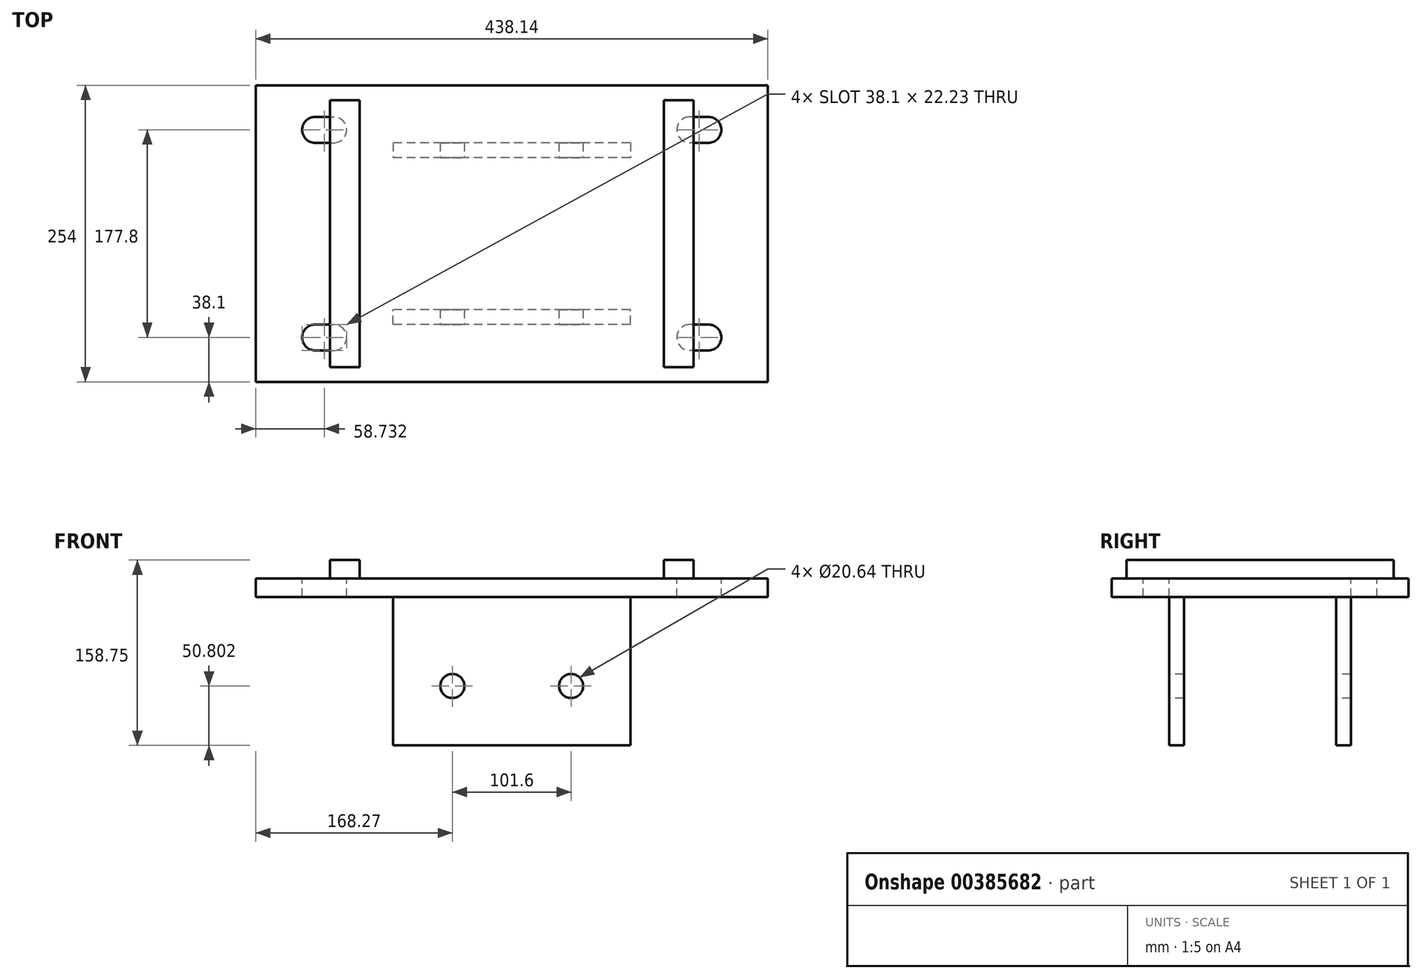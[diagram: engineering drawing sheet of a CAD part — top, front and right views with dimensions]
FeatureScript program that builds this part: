
annotation { "Feature Type Name" : "Feature", "Feature Type Description" : "" }
export const myFeature = defineFeature(function(context is Context, id is Id, definition is map)
    precondition{}
    {
        {
            var Q0;
            Q0=qCreatedBy(makeId("Top.planeOp"),FACE);
            var sketch = newSketch(context, id + "F0", { "sketchPlane" : qUnion([Q0])});
            skLineSegment(sketch, "E0.bottom", {"start": v(219.08, -127) * mm, "end": v(-219.08, -127) * mm});
            skLineSegment(sketch, "E0.top", {"start": v(219.08, 127) * mm, "end": v(-219.08, 127) * mm});
            skLineSegment(sketch, "E0.left", {"start": v(219.08, -127) * mm, "end": v(219.08, 127) * mm});
            skLineSegment(sketch, "E0.right", {"start": v(-219.08, -127) * mm, "end": v(-219.08, 127) * mm});
            skPoint(sketch, "E0.middle", {"position": v(0, 0) * mm});
            skSolve(sketch);
        }
        {
            var Q0;
            Q0 = qSketchRegion(id + "F0", true);
            extrude(context, id + "F1", {"entities" : qUnion([Q0]), "endBound" : BoundingType.SYMMETRIC, "depth" : 15.88 * mm});
        }
        {
            var Q0;
            Q0=qCreatedBy(makeId("Front.planeOp"),FACE);
            var sketch = newSketch(context, id + "F2", { "sketchPlane" : qUnion([Q0])});
            skLineSegment(sketch, "E1.0", {"start": v(219.08, -7.94) * mm, "end": v(-219.08, -7.94) * mm});
            skLineSegment(sketch, "E2.bottom", {"start": v(-101.6, -7.94) * mm, "end": v(101.6, -7.94) * mm});
            skLineSegment(sketch, "E2.top", {"start": v(-101.6, -134.94) * mm, "end": v(101.6, -134.94) * mm});
            skLineSegment(sketch, "E2.left", {"start": v(-101.6, -7.94) * mm, "end": v(-101.6, -134.94) * mm});
            skLineSegment(sketch, "E2.right", {"start": v(101.6, -7.94) * mm, "end": v(101.6, -134.94) * mm});
            skSolve(sketch);
        }
        {
            var Q0;
            Q0 = qSketchRegion(id + "F2", true);
            extrude(context, id + "F3", {"entities" : qUnion([Q0]), "endBound" : BoundingType.SYMMETRIC, "depth" : 12.7 * mm});
        }
        {
            var Q0;
            Q0=makeQuery(id+"F3.opExtrude","SWEPT_BODY",BODY,{"disambiguationData":[OSD([sQuery(id+"F2.wireOp",EDGE,"E2.bottom"),sQuery(id+"F2.wireOp",EDGE,"E2.top"),sQuery(id+"F2.wireOp",EDGE,"E2.left"),sQuery(id+"F2.wireOp",EDGE,"E2.right")])]});
            var Q1;
            Q1=makeQuery(id+"F1.opExtrude","CAP_EDGE",EDGE,{"disambiguationData":[OSD([sQuery(id+"F0.wireOp",EDGE,"E0.left")])],"isStart":true});
            transform(context, id + "F4", {"entities" : qUnion([Q0]), "transformType" : TransformType.TRANSLATION_DISTANCE, "transformDirection" : qUnion([Q1]), "distance" : 71.44 * mm, "oppositeDirection" : true, "makeCopy" : false});
        }
        {
            var Q0;
            Q0=qCreatedBy(makeId("Right.planeOp"),FACE);
            var sketch = newSketch(context, id + "F5", { "sketchPlane" : qUnion([Q0])});
            skLineSegment(sketch, "E3", {"start": v(0, 0) * mm, "end": v(0, 158.38) * mm, "construction": true});
            skSolve(sketch);
        }
        {
            var Q0;
            Q0=makeQuery(id+"F3.opExtrude","SWEPT_BODY",BODY,{"disambiguationData":[OSD([sQuery(id+"F2.wireOp",EDGE,"E2.bottom"),sQuery(id+"F2.wireOp",EDGE,"E2.top"),sQuery(id+"F2.wireOp",EDGE,"E2.left"),sQuery(id+"F2.wireOp",EDGE,"E2.right")])]});
            var Q1;
            Q1=qCreatedBy(makeId("Front.planeOp"),FACE);
            mirror(context, id + "F6", {"operationType" : NewBodyOperationType.ADD, "entities" : qUnion([Q0]), "mirrorPlane" : qUnion([Q1])});
        }
        {
            var Q0;
            Q0=makeQuery(id+"F1.opExtrude","CAP_FACE",FACE,{"disambiguationData":[OSD([sQuery(id+"F0.wireOp",EDGE,"E0.bottom"),sQuery(id+"F0.wireOp",EDGE,"E0.top"),sQuery(id+"F0.wireOp",EDGE,"E0.left"),sQuery(id+"F0.wireOp",EDGE,"E0.right")])],"isStart":false});
            var sketch = newSketch(context, id + "F7", { "sketchPlane" : qUnion([Q0])});
            skLineSegment(sketch, "E4.bottom", {"start": v(-155.58, 114.3) * mm, "end": v(-130.18, 114.3) * mm});
            skLineSegment(sketch, "E4.top", {"start": v(-155.57, -114.3) * mm, "end": v(-130.17, -114.3) * mm});
            skLineSegment(sketch, "E4.left", {"start": v(-155.58, 114.3) * mm, "end": v(-155.58, -114.3) * mm});
            skLineSegment(sketch, "E4.right", {"start": v(-130.18, 114.3) * mm, "end": v(-130.18, -114.3) * mm});
            skLineSegment(sketch, "E5.MirrorCS", {"start": v(155.58, 114.3) * mm, "end": v(130.18, 114.3) * mm});
            skLineSegment(sketch, "E6.MirrorCS", {"start": v(130.18, 114.3) * mm, "end": v(130.18, -114.3) * mm});
            skLineSegment(sketch, "E7.MirrorCS", {"start": v(155.57, -114.3) * mm, "end": v(130.17, -114.3) * mm});
            skLineSegment(sketch, "E8.MirrorCS", {"start": v(155.58, 114.3) * mm, "end": v(155.58, -114.3) * mm});
            skSolve(sketch);
        }
        {
            var Q0;
            Q0 = qSketchRegion(id + "F7", true);
            extrude(context, id + "F8", {"entities" : qUnion([Q0]), "depth" : 15.88 * mm});
        }
        {
            var Q0;
            Q0=makeQuery(id+"F1.opExtrude","CAP_FACE",FACE,{"disambiguationData":[OSD([sQuery(id+"F0.wireOp",EDGE,"E0.bottom"),sQuery(id+"F0.wireOp",EDGE,"E0.top"),sQuery(id+"F0.wireOp",EDGE,"E0.left"),sQuery(id+"F0.wireOp",EDGE,"E0.right")])],"isStart":false});
            var sketch = newSketch(context, id + "F9", { "sketchPlane" : qUnion([Q0])});
            skArc(sketch, "E9", {"start": v(-168.28, -77.79) * mm, "mid": v(-179.39, -88.9) * mm, "end": v(-168.28, -100.01) * mm});
            skArc(sketch, "E10", {"start": v(-152.4, -100.01) * mm, "mid": v(-141.29, -88.9) * mm, "end": v(-152.4, -77.79) * mm});
            skLineSegment(sketch, "E11", {"start": v(-168.28, -77.79) * mm, "end": v(-152.4, -77.79) * mm});
            skLineSegment(sketch, "E12", {"start": v(-168.28, -100.01) * mm, "end": v(-152.4, -100.01) * mm});
            skLineSegment(sketch, "E13", {"start": v(-160.34, -77.79) * mm, "end": v(-160.34, -69.58) * mm, "construction": true});
            skArc(sketch, "E14.MirrorCS", {"start": v(-168.28, 77.79) * mm, "mid": v(-179.39, 88.9) * mm, "end": v(-168.28, 100.01) * mm});
            skLineSegment(sketch, "E15.MirrorCS", {"start": v(-168.28, 77.79) * mm, "end": v(-152.4, 77.79) * mm});
            skLineSegment(sketch, "E16.MirrorCS", {"start": v(-160.34, 77.79) * mm, "end": v(-160.34, 69.58) * mm, "construction": true});
            skArc(sketch, "E17.MirrorCS", {"start": v(-152.4, 100.01) * mm, "mid": v(-141.29, 88.9) * mm, "end": v(-152.4, 77.79) * mm});
            skLineSegment(sketch, "E18.MirrorCS", {"start": v(-168.28, 100.01) * mm, "end": v(-152.4, 100.01) * mm});
            skArc(sketch, "E19.MirrorCS", {"start": v(168.28, 77.79) * mm, "mid": v(179.39, 88.9) * mm, "end": v(168.28, 100.01) * mm});
            skLineSegment(sketch, "E20.MirrorCS", {"start": v(168.28, 77.79) * mm, "end": v(152.4, 77.79) * mm});
            skLineSegment(sketch, "E21.MirrorCS", {"start": v(168.28, -77.79) * mm, "end": v(152.4, -77.79) * mm});
            skLineSegment(sketch, "E22.MirrorCS", {"start": v(160.34, -77.79) * mm, "end": v(160.34, -69.58) * mm, "construction": true});
            skLineSegment(sketch, "E23.MirrorCS", {"start": v(168.28, 100.01) * mm, "end": v(152.4, 100.01) * mm});
            skArc(sketch, "E24.MirrorCS", {"start": v(152.4, 100.01) * mm, "mid": v(141.29, 88.9) * mm, "end": v(152.4, 77.79) * mm});
            skLineSegment(sketch, "E25.MirrorCS", {"start": v(160.34, 77.79) * mm, "end": v(160.34, 69.58) * mm, "construction": true});
            skArc(sketch, "E26.MirrorCS", {"start": v(152.4, -100.01) * mm, "mid": v(141.29, -88.9) * mm, "end": v(152.4, -77.79) * mm});
            skArc(sketch, "E27.MirrorCS", {"start": v(168.28, -77.79) * mm, "mid": v(179.39, -88.9) * mm, "end": v(168.28, -100.01) * mm});
            skLineSegment(sketch, "E28.MirrorCS", {"start": v(168.28, -100.01) * mm, "end": v(152.4, -100.01) * mm});
            skSolve(sketch);
        }
        {
            var Q0;
            Q0 = qSketchRegion(id + "F9", true);
            extrude(context, id + "F10", {"entities" : qUnion([Q0]), "operationType" : NewBodyOperationType.REMOVE, "endBound" : BoundingType.THROUGH_ALL, "oppositeDirection" : true, "depth" : 25.4 * mm});
        }
        {
            var Q0;
            Q0=makeQuery(id+"F3.opExtrude","CAP_FACE",FACE,{"disambiguationData":[OSD([sQuery(id+"F2.wireOp",EDGE,"E2.bottom"),sQuery(id+"F2.wireOp",EDGE,"E2.top"),sQuery(id+"F2.wireOp",EDGE,"E2.left"),sQuery(id+"F2.wireOp",EDGE,"E2.right")])],"isStart":false});
            var sketch = newSketch(context, id + "F11", { "sketchPlane" : qUnion([Q0])});
            skCircle(sketch, "E29", {"center": v(-50.8, -84.14) * mm, "radius": 10.32 * mm});
            skCircle(sketch, "E30.MirrorC", {"center": v(50.8, -84.14) * mm, "radius": 10.32 * mm});
            skSolve(sketch);
        }
        {
            var Q0;
            Q0 = qSketchRegion(id + "F11", true);
            extrude(context, id + "F12", {"entities" : qUnion([Q0]), "operationType" : NewBodyOperationType.REMOVE, "endBound" : BoundingType.THROUGH_ALL, "oppositeDirection" : true, "depth" : 25.4 * mm});
        }
    });
